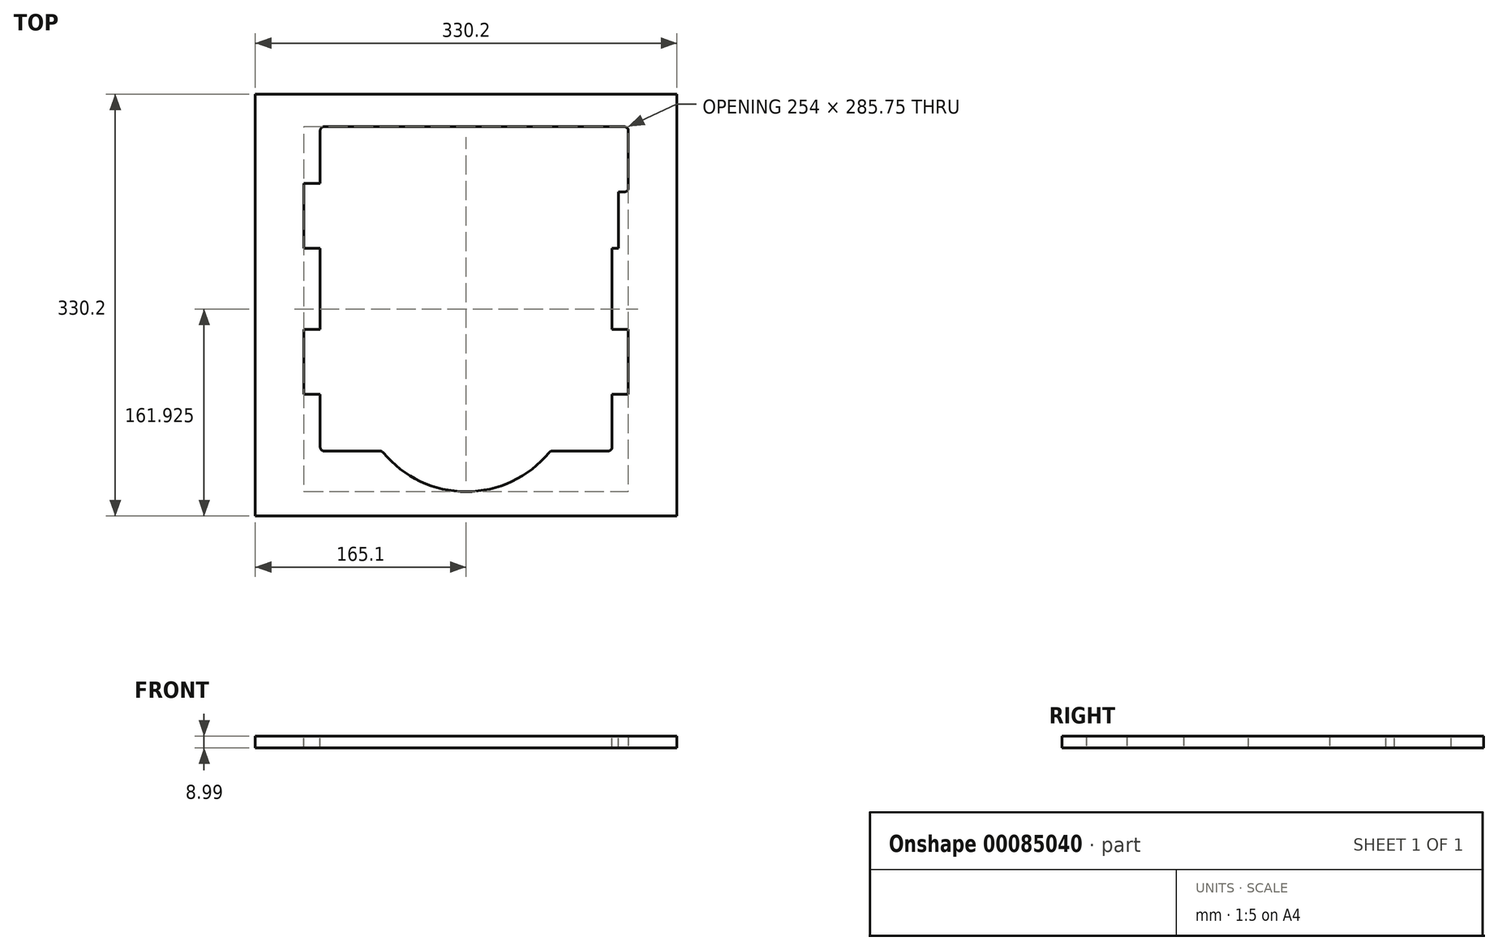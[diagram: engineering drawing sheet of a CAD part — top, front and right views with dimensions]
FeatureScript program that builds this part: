
annotation { "Feature Type Name" : "Feature", "Feature Type Description" : "" }
export const myFeature = defineFeature(function(context is Context, id is Id, definition is map)
    precondition{}
    {
        {
            var Q0;
            Q0=qCreatedBy(makeId("Top.planeOp"),FACE);
            var sketch = newSketch(context, id + "F0", { "sketchPlane" : qUnion([Q0])});
            skLineSegment(sketch, "E0.bottom", {"start": v(111.13, -114.3) * mm, "end": v(67.4, -114.3) * mm});
            skLineSegment(sketch, "E0.top", {"start": v(114.3, 114.3) * mm, "end": v(-111.13, 114.3) * mm});
            skLineSegment(sketch, "E0.left", {"start": v(114.3, -111.13) * mm, "end": v(114.3, 85.34) * mm});
            skLineSegment(sketch, "E0.right", {"start": v(-114.3, -111.13) * mm, "end": v(-114.3, 111.13) * mm});
            skPoint(sketch, "E0.middle", {"position": v(0, 0) * mm});
            skLineSegment(sketch, "E1.bottom", {"start": v(114.3, 114.3) * mm, "end": v(123.83, 114.3) * mm});
            skLineSegment(sketch, "E1.top", {"start": v(117.47, 88.52) * mm, "end": v(123.83, 88.52) * mm});
            skLineSegment(sketch, "E1.right", {"start": v(127, 111.13) * mm, "end": v(127, 91.7) * mm});
            skArc(sketch, "E2", {"start": v(-64.95, -115.45) * mm, "mid": v(0, -146.05) * mm, "end": v(64.95, -115.45) * mm});
            skLineSegment(sketch, "E3.trimOffspring", {"start": v(-67.4, -114.3) * mm, "end": v(-111.13, -114.3) * mm});
            skPoint(sketch, "E4.visualSharp", {"position": v(127, 114.3) * mm});
            skArc(sketch, "E4.filletArc", {"start": v(127, 111.13) * mm, "mid": v(126.07, 113.37) * mm, "end": v(123.83, 114.3) * mm});
            skPoint(sketch, "E5.visualSharp", {"position": v(127, 88.52) * mm});
            skArc(sketch, "E5.filletArc", {"start": v(123.83, 88.52) * mm, "mid": v(126.07, 89.45) * mm, "end": v(127, 91.7) * mm});
            skPoint(sketch, "E6.visualSharp", {"position": v(-114.3, 114.3) * mm});
            skArc(sketch, "E6.filletArc", {"start": v(-111.13, 114.3) * mm, "mid": v(-113.37, 113.37) * mm, "end": v(-114.3, 111.13) * mm});
            skPoint(sketch, "E7.visualSharp", {"position": v(-114.3, -114.3) * mm});
            skArc(sketch, "E7.filletArc", {"start": v(-114.3, -111.13) * mm, "mid": v(-113.37, -113.37) * mm, "end": v(-111.13, -114.3) * mm});
            skPoint(sketch, "E8.visualSharp", {"position": v(-65.88, -114.3) * mm});
            skArc(sketch, "E8.filletArc", {"start": v(-64.95, -115.45) * mm, "mid": v(-66.04, -114.6) * mm, "end": v(-67.4, -114.3) * mm});
            skPoint(sketch, "E9.visualSharp", {"position": v(65.88, -114.3) * mm});
            skArc(sketch, "E9.filletArc", {"start": v(67.4, -114.3) * mm, "mid": v(66.04, -114.6) * mm, "end": v(64.95, -115.45) * mm});
            skPoint(sketch, "E10.visualSharp", {"position": v(114.3, -114.3) * mm});
            skArc(sketch, "E10.filletArc", {"start": v(111.13, -114.3) * mm, "mid": v(113.37, -113.37) * mm, "end": v(114.3, -111.13) * mm});
            skPoint(sketch, "E11.visualSharp", {"position": v(114.3, 88.52) * mm});
            skArc(sketch, "E11.filletArc", {"start": v(117.47, 88.52) * mm, "mid": v(115.23, 87.59) * mm, "end": v(114.3, 85.34) * mm});
            skSolve(sketch);
        }
        {
            var Q0;
            Q0=makeQuery(id+"F0.imprint","IMPRINT",FACE,{"disambiguationData":[TD([[makeQuery(id+"F0.imprint","IMPRINT",EDGE,{"derivedFrom":sQuery(id+"F0.wireOp",EDGE,"E0.bottom")}),-1.0]])]});
            extrude(context, id + "F1", {"entities" : qUnion([Q0]), "depth" : 8.9 * mm});
        }
        {
            var Q0;
            Q0=makeQuery(id+"F1.opExtrude","SWEPT_FACE",FACE,{"disambiguationData":[OSD([sQuery(id+"F0.wireOp",EDGE,"E0.left")])]});
            var sketch = newSketch(context, id + "F2", { "sketchPlane" : qUnion([Q0])});
            skPoint(sketch, "E12.0", {"position": v(114.3, 0) * mm});
            skLineSegment(sketch, "E13", {"start": v(114.3, 0) * mm, "end": v(111.12, 0) * mm, "construction": true});
            skLineSegment(sketch, "E14", {"start": v(66.68, -3.18) * mm, "end": v(50.8, -3.18) * mm});
            skLineSegment(sketch, "E15", {"start": v(50.8, -3.17) * mm, "end": v(44.45, 0) * mm});
            skLineSegment(sketch, "E16", {"start": v(66.68, -3.17) * mm, "end": v(69.85, -4.76) * mm});
            skLineSegment(sketch, "E17.0", {"start": v(-111.13, 0) * mm, "end": v(44.45, 0) * mm});
            skPoint(sketch, "E18.orphan", {"position": v(111.12, 0) * mm});
            skLineSegment(sketch, "E19.0", {"start": v(51.4, -0.64) * mm, "end": v(44.45, 2.84) * mm});
            skLineSegment(sketch, "E19.1", {"start": v(67.27, -0.63) * mm, "end": v(51.4, -0.64) * mm});
            skLineSegment(sketch, "E19.2", {"start": v(67.27, -0.63) * mm, "end": v(69.85, -1.92) * mm});
            skLineSegment(sketch, "E20", {"start": v(44.45, 0) * mm, "end": v(44.45, 2.84) * mm});
            skLineSegment(sketch, "E21", {"start": v(69.85, -4.76) * mm, "end": v(69.85, -1.92) * mm});
            skSolve(sketch);
        }
        {
            var Q0;
            Q0=makeQuery(id+"F2.imprint","IMPRINT",FACE,{"disambiguationData":[TD([[makeQuery(id+"F2.imprint","IMPRINT",EDGE,{"derivedFrom":sQuery(id+"F2.wireOp",EDGE,"E14")}),-1.0]])]});
            var Q1;
            {var subQ0=sQuery(id+"F2.wireOp",EDGE,"E20");Q1=makeQuery(id+"F2.imprint","IMPRINT",FACE,{"disambiguationData":[TD([[makeQuery(id+"F2.imprint","IMPRINT",EDGE,{"derivedFrom":subQ0}),-1.0]])]});}
            extrude(context, id + "F3", {"entities" : qUnion([Q0, Q1]), "depth" : 4.93 * mm, "hasSecondDirection" : true, "secondDirectionOppositeDirection" : true, "secondDirectionDepth" : 2.54 * mm});
        }
        {
            var Q0;
            Q0=makeQuery(id+"F3.opExtrude","SWEPT_BODY",BODY,{"disambiguationData":[OSD([sQuery(id+"F0.wireOp",EDGE,"E0.left"),sQuery(id+"F2.wireOp",EDGE,"E14"),sQuery(id+"F2.wireOp",EDGE,"E15"),sQuery(id+"F2.wireOp",EDGE,"E16"),sQuery(id+"F2.wireOp",EDGE,"E19.0"),sQuery(id+"F2.wireOp",EDGE,"E19.1"),sQuery(id+"F2.wireOp",EDGE,"E19.2"),sQuery(id+"F2.wireOp",EDGE,"E21")])]});
            transform(context, id + "F4", {"entities" : qUnion([Q0]), "transformType" : TransformType.TRANSLATION_3D, "dx" : 0 * mm, "dy" : -114.3 * mm, "dz" : 0 * mm, "makeCopy" : true});
        }
        {
            var Q0;
            Q0=makeQuery(id+"F3.opExtrude","SWEPT_BODY",BODY,{"disambiguationData":[OSD([sQuery(id+"F0.wireOp",EDGE,"E0.left"),sQuery(id+"F2.wireOp",EDGE,"E14"),sQuery(id+"F2.wireOp",EDGE,"E15"),sQuery(id+"F2.wireOp",EDGE,"E16"),sQuery(id+"F2.wireOp",EDGE,"E19.0"),sQuery(id+"F2.wireOp",EDGE,"E19.1"),sQuery(id+"F2.wireOp",EDGE,"E19.2"),sQuery(id+"F2.wireOp",EDGE,"E21")])]});
            var Q1;
            Q1=makeQuery(id+"F4.opPattern","COPY",BODY,{"derivedFrom":makeQuery(id+"F3.opExtrude","SWEPT_BODY",BODY,{"disambiguationData":[OSD([sQuery(id+"F0.wireOp",EDGE,"E0.left"),sQuery(id+"F2.wireOp",EDGE,"E14"),sQuery(id+"F2.wireOp",EDGE,"E15"),sQuery(id+"F2.wireOp",EDGE,"E16"),sQuery(id+"F2.wireOp",EDGE,"E19.0"),sQuery(id+"F2.wireOp",EDGE,"E19.1"),sQuery(id+"F2.wireOp",EDGE,"E19.2"),sQuery(id+"F2.wireOp",EDGE,"E21")])]}),"instanceName":"1"});
            var Q2;
            Q2=qCreatedBy(makeId("Right.planeOp"),FACE);
            mirror(context, id + "F5", {"operationType" : NewBodyOperationType.ADD, "entities" : qUnion([Q0, Q1]), "mirrorPlane" : qUnion([Q2])});
        }
        {
            var Q0;
            Q0=makeQuery(id+"F1.opExtrude","CAP_FACE",FACE,{"disambiguationData":[OSD([sQuery(id+"F0.wireOp",EDGE,"E0.bottom"),sQuery(id+"F0.wireOp",EDGE,"E0.top"),sQuery(id+"F0.wireOp",EDGE,"E0.left"),sQuery(id+"F0.wireOp",EDGE,"E0.right"),sQuery(id+"F0.wireOp",EDGE,"E1.bottom"),sQuery(id+"F0.wireOp",EDGE,"E1.top"),sQuery(id+"F0.wireOp",EDGE,"E1.right"),sQuery(id+"F0.wireOp",EDGE,"E2"),sQuery(id+"F0.wireOp",EDGE,"E3.trimOffspring"),sQuery(id+"F0.wireOp",EDGE,"E4.filletArc"),sQuery(id+"F0.wireOp",EDGE,"E5.filletArc"),sQuery(id+"F0.wireOp",EDGE,"E6.filletArc"),sQuery(id+"F0.wireOp",EDGE,"E7.filletArc"),sQuery(id+"F0.wireOp",EDGE,"E8.filletArc"),sQuery(id+"F0.wireOp",EDGE,"E9.filletArc"),sQuery(id+"F0.wireOp",EDGE,"E10.filletArc"),sQuery(id+"F0.wireOp",EDGE,"E11.filletArc")])],"isStart":false});
            var sketch = newSketch(context, id + "F6", { "sketchPlane" : qUnion([Q0])});
            skLineSegment(sketch, "E22", {"start": v(-33.2, -114.3) * mm, "end": v(33.2, -114.3) * mm});
            skLineSegment(sketch, "E23", {"start": v(0, -114.3) * mm, "end": v(0, -138.11) * mm, "construction": true});
            skPoint(sketch, "E23.endSnap0", {"position": v(0, -114.3) * mm});
            skArc(sketch, "E24", {"start": v(-36.66, -122.34) * mm, "mid": v(0, -138.11) * mm, "end": v(36.66, -122.34) * mm});
            skPoint(sketch, "E25.visualSharp", {"position": v(-42.86, -114.3) * mm});
            skArc(sketch, "E25.filletArc", {"start": v(-33.2, -114.3) * mm, "mid": v(-37.58, -117.18) * mm, "end": v(-36.66, -122.34) * mm});
            skPoint(sketch, "E26.visualSharp", {"position": v(42.86, -114.3) * mm});
            skArc(sketch, "E26.filletArc", {"start": v(36.66, -122.34) * mm, "mid": v(37.58, -117.18) * mm, "end": v(33.2, -114.3) * mm});
            skSolve(sketch);
        }
        {
            var Q0;
            Q0=makeQuery(id+"F6.imprint","IMPRINT",FACE,{"disambiguationData":[TD([[makeQuery(id+"F6.imprint","IMPRINT",EDGE,{"derivedFrom":sQuery(id+"F6.wireOp",EDGE,"E22")}),-1.0]])]});
            extrude(context, id + "F7", {"entities" : qUnion([Q0]), "operationType" : NewBodyOperationType.REMOVE, "endBound" : BoundingType.THROUGH_ALL, "oppositeDirection" : true, "depth" : 25.4 * mm});
        }
        {
            var Q0;
            Q0=qCreatedBy(makeId("Top.planeOp"),FACE);
            var sketch = newSketch(context, id + "F8", { "sketchPlane" : qUnion([Q0])});
            skLineSegment(sketch, "E27.bottom", {"start": v(165.1, -165.1) * mm, "end": v(-165.1, -165.1) * mm});
            skLineSegment(sketch, "E27.top", {"start": v(165.1, 165.1) * mm, "end": v(-165.1, 165.1) * mm});
            skLineSegment(sketch, "E27.left", {"start": v(165.1, -165.1) * mm, "end": v(165.1, 165.1) * mm});
            skLineSegment(sketch, "E27.right", {"start": v(-165.1, -165.1) * mm, "end": v(-165.1, 165.1) * mm});
            skPoint(sketch, "E27.middle", {"position": v(0, 0) * mm});
            skLineSegment(sketch, "E28.0", {"start": v(-111.13, 114.3) * mm, "end": v(123.83, 114.3) * mm});
            skArc(sketch, "E29.0", {"start": v(-111.13, 114.3) * mm, "mid": v(-113.37, 113.37) * mm, "end": v(-114.3, 111.13) * mm});
            skLineSegment(sketch, "E30.0", {"start": v(-114.3, -111.13) * mm, "end": v(-114.3, 111.13) * mm});
            skLineSegment(sketch, "E31.0", {"start": v(-119.23, 69.85) * mm, "end": v(-114.3, 69.85) * mm});
            skLineSegment(sketch, "E32.0", {"start": v(-119.23, 67.27) * mm, "end": v(-119.23, 69.85) * mm});
            skLineSegment(sketch, "E33.0", {"start": v(-119.23, 67.27) * mm, "end": v(-119.23, 51.4) * mm});
            skLineSegment(sketch, "E34.0", {"start": v(-119.23, 51.4) * mm, "end": v(-119.23, 44.45) * mm});
            skLineSegment(sketch, "E35.0", {"start": v(-119.23, 44.45) * mm, "end": v(-114.3, 44.45) * mm});
            skLineSegment(sketch, "E36.0", {"start": v(-119.23, -44.45) * mm, "end": v(-114.3, -44.45) * mm});
            skLineSegment(sketch, "E37.0", {"start": v(-119.23, -47.03) * mm, "end": v(-119.23, -44.45) * mm});
            skLineSegment(sketch, "E38.0", {"start": v(-119.23, -47.03) * mm, "end": v(-119.23, -62.9) * mm});
            skLineSegment(sketch, "E39.0", {"start": v(-119.23, -62.9) * mm, "end": v(-119.23, -69.85) * mm});
            skLineSegment(sketch, "E40.0", {"start": v(-119.23, -69.85) * mm, "end": v(-114.3, -69.85) * mm});
            skArc(sketch, "E41.0", {"start": v(-114.3, -111.13) * mm, "mid": v(-113.37, -113.37) * mm, "end": v(-111.13, -114.3) * mm});
            skLineSegment(sketch, "E42.0", {"start": v(-67.4, -114.3) * mm, "end": v(-111.13, -114.3) * mm});
            skArc(sketch, "E43.0", {"start": v(-64.95, -115.45) * mm, "mid": v(0, -146.05) * mm, "end": v(64.95, -115.45) * mm});
            skArc(sketch, "E44.0", {"start": v(67.4, -114.3) * mm, "mid": v(66.04, -114.6) * mm, "end": v(64.95, -115.45) * mm});
            skLineSegment(sketch, "E45.0", {"start": v(111.13, -114.3) * mm, "end": v(67.4, -114.3) * mm});
            skArc(sketch, "E46.0", {"start": v(111.13, -114.3) * mm, "mid": v(113.37, -113.37) * mm, "end": v(114.3, -111.13) * mm});
            skLineSegment(sketch, "E47.0", {"start": v(114.3, -111.13) * mm, "end": v(114.3, 85.34) * mm});
            skLineSegment(sketch, "E48.0", {"start": v(119.23, -69.85) * mm, "end": v(114.3, -69.85) * mm});
            skLineSegment(sketch, "E49.0", {"start": v(119.23, -62.9) * mm, "end": v(119.23, -69.85) * mm});
            skLineSegment(sketch, "E50.0", {"start": v(119.23, -47.03) * mm, "end": v(119.23, -62.9) * mm});
            skLineSegment(sketch, "E51.0", {"start": v(119.23, -47.03) * mm, "end": v(119.23, -44.45) * mm});
            skLineSegment(sketch, "E52.0", {"start": v(119.23, -44.45) * mm, "end": v(114.3, -44.45) * mm});
            skLineSegment(sketch, "E53.0", {"start": v(119.23, 44.45) * mm, "end": v(114.3, 44.45) * mm});
            skLineSegment(sketch, "E54.0", {"start": v(119.23, 51.4) * mm, "end": v(119.23, 44.45) * mm});
            skLineSegment(sketch, "E55.0", {"start": v(119.23, 67.27) * mm, "end": v(119.23, 51.4) * mm});
            skLineSegment(sketch, "E56.0", {"start": v(119.23, 67.27) * mm, "end": v(119.23, 69.85) * mm});
            skLineSegment(sketch, "E57.0", {"start": v(119.23, 69.85) * mm, "end": v(114.3, 69.85) * mm});
            skArc(sketch, "E58.0", {"start": v(117.47, 88.52) * mm, "mid": v(115.23, 87.59) * mm, "end": v(114.3, 85.34) * mm});
            skLineSegment(sketch, "E59.0", {"start": v(117.47, 88.52) * mm, "end": v(123.83, 88.52) * mm});
            skArc(sketch, "E60.0", {"start": v(123.83, 88.52) * mm, "mid": v(126.07, 89.45) * mm, "end": v(127, 91.7) * mm});
            skLineSegment(sketch, "E61.0", {"start": v(127, 111.13) * mm, "end": v(127, 91.7) * mm});
            skArc(sketch, "E62.0", {"start": v(127, 111.13) * mm, "mid": v(126.07, 113.37) * mm, "end": v(123.83, 114.3) * mm});
            skPoint(sketch, "E63.orphan", {"position": v(-111.76, 69.85) * mm});
            skPoint(sketch, "E64.orphan", {"position": v(111.76, 69.85) * mm});
            skPoint(sketch, "E65.orphan", {"position": v(111.76, -44.45) * mm});
            skPoint(sketch, "E66.orphan", {"position": v(-111.76, -44.45) * mm});
            skPoint(sketch, "E67.orphan", {"position": v(-111.76, -62.9) * mm});
            skArc(sketch, "E68.0", {"start": v(-64.95, -115.45) * mm, "mid": v(-66.04, -114.6) * mm, "end": v(-67.4, -114.3) * mm});
            skSolve(sketch);
        }
        {
            var Q0;
            Q0=makeQuery(id+"F8.imprint","IMPRINT",FACE,{"disambiguationData":[TD([[makeQuery(id+"F8.imprint","IMPRINT",EDGE,{"derivedFrom":sQuery(id+"F8.wireOp",EDGE,"E27.bottom")}),-1.0]])]});
            extrude(context, id + "F9", {"entities" : qUnion([Q0]), "depth" : 9 * mm});
        }
        {
            var Q0;
            Q0=makeQuery(id+"F1.opExtrude","SWEPT_BODY",BODY,{"disambiguationData":[OSD([sQuery(id+"F0.wireOp",EDGE,"E0.bottom"),sQuery(id+"F0.wireOp",EDGE,"E0.top"),sQuery(id+"F0.wireOp",EDGE,"E0.left"),sQuery(id+"F0.wireOp",EDGE,"E0.right"),sQuery(id+"F0.wireOp",EDGE,"E1.bottom"),sQuery(id+"F0.wireOp",EDGE,"E1.top"),sQuery(id+"F0.wireOp",EDGE,"E1.right"),sQuery(id+"F0.wireOp",EDGE,"E2"),sQuery(id+"F0.wireOp",EDGE,"E3.trimOffspring"),sQuery(id+"F0.wireOp",EDGE,"E4.filletArc"),sQuery(id+"F0.wireOp",EDGE,"E5.filletArc"),sQuery(id+"F0.wireOp",EDGE,"E6.filletArc"),sQuery(id+"F0.wireOp",EDGE,"E7.filletArc"),sQuery(id+"F0.wireOp",EDGE,"E8.filletArc"),sQuery(id+"F0.wireOp",EDGE,"E9.filletArc"),sQuery(id+"F0.wireOp",EDGE,"E10.filletArc"),sQuery(id+"F0.wireOp",EDGE,"E11.filletArc")])]});
            transform(context, id + "F10", {"entities" : qUnion([Q0]), "transformType" : TransformType.TRANSLATION_3D, "dx" : 0 * mm, "dy" : 25.4 * mm, "dz" : 0 * mm, "makeCopy" : false});
        }
        {
            var Q0;
            Q0=makeQuery(id+"F9.opExtrude","CAP_FACE",FACE,{"disambiguationData":[OSD([sQuery(id+"F8.wireOp",EDGE,"E27.bottom"),sQuery(id+"F8.wireOp",EDGE,"E27.top"),sQuery(id+"F8.wireOp",EDGE,"E27.left"),sQuery(id+"F8.wireOp",EDGE,"E27.right"),sQuery(id+"F8.wireOp",EDGE,"E28.0"),sQuery(id+"F8.wireOp",EDGE,"E29.0"),sQuery(id+"F8.wireOp",EDGE,"E30.0"),sQuery(id+"F8.wireOp",EDGE,"E31.0"),sQuery(id+"F8.wireOp",EDGE,"E32.0"),sQuery(id+"F8.wireOp",EDGE,"E33.0"),sQuery(id+"F8.wireOp",EDGE,"E34.0"),sQuery(id+"F8.wireOp",EDGE,"E35.0"),sQuery(id+"F8.wireOp",EDGE,"E36.0"),sQuery(id+"F8.wireOp",EDGE,"E37.0"),sQuery(id+"F8.wireOp",EDGE,"E38.0"),sQuery(id+"F8.wireOp",EDGE,"E39.0"),sQuery(id+"F8.wireOp",EDGE,"E40.0"),sQuery(id+"F8.wireOp",EDGE,"E41.0"),sQuery(id+"F8.wireOp",EDGE,"E42.0"),sQuery(id+"F8.wireOp",EDGE,"E43.0"),sQuery(id+"F8.wireOp",EDGE,"E44.0"),sQuery(id+"F8.wireOp",EDGE,"E45.0"),sQuery(id+"F8.wireOp",EDGE,"E46.0"),sQuery(id+"F8.wireOp",EDGE,"E47.0"),sQuery(id+"F8.wireOp",EDGE,"E48.0"),sQuery(id+"F8.wireOp",EDGE,"E49.0"),sQuery(id+"F8.wireOp",EDGE,"E50.0"),sQuery(id+"F8.wireOp",EDGE,"E51.0"),sQuery(id+"F8.wireOp",EDGE,"E52.0"),sQuery(id+"F8.wireOp",EDGE,"E53.0"),sQuery(id+"F8.wireOp",EDGE,"E54.0"),sQuery(id+"F8.wireOp",EDGE,"E55.0"),sQuery(id+"F8.wireOp",EDGE,"E56.0"),sQuery(id+"F8.wireOp",EDGE,"E57.0"),sQuery(id+"F8.wireOp",EDGE,"E58.0"),sQuery(id+"F8.wireOp",EDGE,"E59.0"),sQuery(id+"F8.wireOp",EDGE,"E60.0"),sQuery(id+"F8.wireOp",EDGE,"E61.0"),sQuery(id+"F8.wireOp",EDGE,"E62.0"),sQuery(id+"F8.wireOp",EDGE,"E68.0")])],"isStart":false});
            var sketch = newSketch(context, id + "F11", { "sketchPlane" : qUnion([Q0])});
            skLineSegment(sketch, "E69.0", {"start": v(117.47, 113.92) * mm, "end": v(123.83, 113.92) * mm});
            skArc(sketch, "E70.0", {"start": v(123.83, 113.92) * mm, "mid": v(126.07, 114.85) * mm, "end": v(127, 117.1) * mm});
            skLineSegment(sketch, "E71.0", {"start": v(127, 136.53) * mm, "end": v(127, 117.1) * mm});
            skArc(sketch, "E72.0", {"start": v(127, 136.53) * mm, "mid": v(126.07, 138.77) * mm, "end": v(123.83, 139.7) * mm});
            skLineSegment(sketch, "E73.0", {"start": v(-111.13, 139.7) * mm, "end": v(123.83, 139.7) * mm});
            skArc(sketch, "E74.0", {"start": v(-111.13, 139.7) * mm, "mid": v(-113.37, 138.77) * mm, "end": v(-114.3, 136.53) * mm});
            skLineSegment(sketch, "E75.0", {"start": v(-114.3, -85.73) * mm, "end": v(-114.3, 136.53) * mm});
            skLineSegment(sketch, "E76.0", {"start": v(-119.23, 95.25) * mm, "end": v(-111.76, 95.25) * mm});
            skLineSegment(sketch, "E77.0", {"start": v(-119.23, 92.67) * mm, "end": v(-119.23, 95.25) * mm});
            skLineSegment(sketch, "E78.0", {"start": v(-119.23, 92.67) * mm, "end": v(-119.23, 76.8) * mm});
            skLineSegment(sketch, "E79.0", {"start": v(-119.23, 76.8) * mm, "end": v(-119.23, 69.85) * mm});
            skLineSegment(sketch, "E80.0", {"start": v(-119.23, 69.85) * mm, "end": v(-114.3, 69.85) * mm});
            skLineSegment(sketch, "E81.0", {"start": v(-119.23, -19.05) * mm, "end": v(-111.76, -19.05) * mm});
            skLineSegment(sketch, "E82.0", {"start": v(-119.23, -21.63) * mm, "end": v(-119.23, -19.05) * mm});
            skLineSegment(sketch, "E83.0", {"start": v(-119.23, -21.63) * mm, "end": v(-119.23, -37.5) * mm});
            skLineSegment(sketch, "E84.0", {"start": v(-119.23, -37.5) * mm, "end": v(-119.23, -44.45) * mm});
            skLineSegment(sketch, "E85.0", {"start": v(-119.23, -44.45) * mm, "end": v(-114.3, -44.45) * mm});
            skLineSegment(sketch, "E86.0", {"start": v(119.23, -44.45) * mm, "end": v(114.3, -44.45) * mm});
            skLineSegment(sketch, "E87.0", {"start": v(119.23, -37.5) * mm, "end": v(119.23, -44.45) * mm});
            skLineSegment(sketch, "E88.0", {"start": v(119.23, -21.63) * mm, "end": v(119.23, -37.5) * mm});
            skLineSegment(sketch, "E89.0", {"start": v(119.23, -21.63) * mm, "end": v(119.23, -19.05) * mm});
            skLineSegment(sketch, "E90.0", {"start": v(119.23, -19.05) * mm, "end": v(111.76, -19.05) * mm});
            skLineSegment(sketch, "E91.0", {"start": v(114.3, -85.73) * mm, "end": v(114.3, 110.74) * mm});
            skLineSegment(sketch, "E92.0", {"start": v(119.23, 69.85) * mm, "end": v(114.3, 69.85) * mm});
            skLineSegment(sketch, "E93.0", {"start": v(119.23, 76.8) * mm, "end": v(119.23, 69.85) * mm});
            skLineSegment(sketch, "E94.0", {"start": v(119.23, 92.67) * mm, "end": v(119.23, 76.8) * mm});
            skLineSegment(sketch, "E95.0", {"start": v(119.23, 92.67) * mm, "end": v(119.23, 95.25) * mm});
            skLineSegment(sketch, "E96.0", {"start": v(119.23, 95.25) * mm, "end": v(111.76, 95.25) * mm});
            skArc(sketch, "E97.0", {"start": v(117.47, 113.92) * mm, "mid": v(115.23, 112.99) * mm, "end": v(114.3, 110.74) * mm});
            skLineSegment(sketch, "E98.0", {"start": v(-67.4, -88.9) * mm, "end": v(-111.13, -88.9) * mm});
            skArc(sketch, "E99.0", {"start": v(-114.3, -85.73) * mm, "mid": v(-113.37, -87.97) * mm, "end": v(-111.13, -88.9) * mm});
            skArc(sketch, "E100.0", {"start": v(-64.95, -90.05) * mm, "mid": v(-66.04, -89.2) * mm, "end": v(-67.4, -88.9) * mm});
            skArc(sketch, "E101.0", {"start": v(-64.95, -90.05) * mm, "mid": v(0, -120.65) * mm, "end": v(64.95, -90.05) * mm});
            skArc(sketch, "E102.0", {"start": v(111.13, -88.9) * mm, "mid": v(113.37, -87.97) * mm, "end": v(114.3, -85.73) * mm});
            skLineSegment(sketch, "E103.0", {"start": v(111.13, -88.9) * mm, "end": v(67.4, -88.9) * mm});
            skArc(sketch, "E104.0", {"start": v(67.4, -88.9) * mm, "mid": v(66.04, -89.2) * mm, "end": v(64.95, -90.05) * mm});
            skSolve(sketch);
        }
        {
            var Q0;
            Q0=makeQuery(id+"F1.opExtrude","SWEPT_BODY",BODY,{"disambiguationData":[OSD([sQuery(id+"F0.wireOp",EDGE,"E0.bottom"),sQuery(id+"F0.wireOp",EDGE,"E0.top"),sQuery(id+"F0.wireOp",EDGE,"E0.left"),sQuery(id+"F0.wireOp",EDGE,"E0.right"),sQuery(id+"F0.wireOp",EDGE,"E1.bottom"),sQuery(id+"F0.wireOp",EDGE,"E1.top"),sQuery(id+"F0.wireOp",EDGE,"E1.right"),sQuery(id+"F0.wireOp",EDGE,"E2"),sQuery(id+"F0.wireOp",EDGE,"E3.trimOffspring"),sQuery(id+"F0.wireOp",EDGE,"E4.filletArc"),sQuery(id+"F0.wireOp",EDGE,"E5.filletArc"),sQuery(id+"F0.wireOp",EDGE,"E6.filletArc"),sQuery(id+"F0.wireOp",EDGE,"E7.filletArc"),sQuery(id+"F0.wireOp",EDGE,"E8.filletArc"),sQuery(id+"F0.wireOp",EDGE,"E9.filletArc"),sQuery(id+"F0.wireOp",EDGE,"E10.filletArc"),sQuery(id+"F0.wireOp",EDGE,"E11.filletArc")])]});
            deleteBodies(context, id + "F12", {"entities" : qUnion([Q0])});
        }
        {
            var Q0;
            {var subQ1=sQuery(id+"F11.wireOp",EDGE,"E71.0");Q0=makeQuery(id+"F11.imprint","IMPRINT",FACE,{"disambiguationData":[TD([[makeQuery(id+"F11.imprint","IMPRINT",EDGE,{"derivedFrom":subQ1}),-1.0]])]});}
            var Q1;
            {var subQ0=sQuery(id+"F11.wireOp",EDGE,"E77.0");Q1=makeQuery(id+"F11.imprint","IMPRINT",FACE,{"disambiguationData":[TD([[makeQuery(id+"F11.imprint","IMPRINT",EDGE,{"derivedFrom":subQ0}),-1.0]])]});}
            var Q2;
            {var subQ0=sQuery(id+"F11.wireOp",EDGE,"E82.0");Q2=makeQuery(id+"F11.imprint","IMPRINT",FACE,{"disambiguationData":[TD([[makeQuery(id+"F11.imprint","IMPRINT",EDGE,{"derivedFrom":subQ0}),-1.0]])]});}
            var Q3;
            {var subQ2=sQuery(id+"F11.wireOp",EDGE,"E86.0");Q3=makeQuery(id+"F11.imprint","IMPRINT",FACE,{"disambiguationData":[TD([[makeQuery(id+"F11.imprint","IMPRINT",EDGE,{"derivedFrom":subQ2}),-1.0]])]});}
            var Q4;
            {var subQ1=sQuery(id+"F11.wireOp",EDGE,"E92.0");Q4=makeQuery(id+"F11.imprint","IMPRINT",FACE,{"disambiguationData":[TD([[makeQuery(id+"F11.imprint","IMPRINT",EDGE,{"derivedFrom":subQ1}),-1.0]])]});}
            extrude(context, id + "F13", {"entities" : qUnion([Q0, Q1, Q2, Q3, Q4]), "operationType" : NewBodyOperationType.REMOVE, "oppositeDirection" : true, "depth" : 25.4 * mm});
        }
        {
            var Q0;
            Q0=makeQuery(id+"F9.opExtrude","CAP_FACE",FACE,{"disambiguationData":[OSD([sQuery(id+"F8.wireOp",EDGE,"E27.bottom"),sQuery(id+"F8.wireOp",EDGE,"E27.top"),sQuery(id+"F8.wireOp",EDGE,"E27.left"),sQuery(id+"F8.wireOp",EDGE,"E27.right"),sQuery(id+"F8.wireOp",EDGE,"E28.0"),sQuery(id+"F8.wireOp",EDGE,"E29.0"),sQuery(id+"F8.wireOp",EDGE,"E30.0"),sQuery(id+"F8.wireOp",EDGE,"E31.0"),sQuery(id+"F8.wireOp",EDGE,"E32.0"),sQuery(id+"F8.wireOp",EDGE,"E33.0"),sQuery(id+"F8.wireOp",EDGE,"E34.0"),sQuery(id+"F8.wireOp",EDGE,"E35.0"),sQuery(id+"F8.wireOp",EDGE,"E36.0"),sQuery(id+"F8.wireOp",EDGE,"E37.0"),sQuery(id+"F8.wireOp",EDGE,"E38.0"),sQuery(id+"F8.wireOp",EDGE,"E39.0"),sQuery(id+"F8.wireOp",EDGE,"E40.0"),sQuery(id+"F8.wireOp",EDGE,"E41.0"),sQuery(id+"F8.wireOp",EDGE,"E42.0"),sQuery(id+"F8.wireOp",EDGE,"E43.0"),sQuery(id+"F8.wireOp",EDGE,"E44.0"),sQuery(id+"F8.wireOp",EDGE,"E45.0"),sQuery(id+"F8.wireOp",EDGE,"E46.0"),sQuery(id+"F8.wireOp",EDGE,"E47.0"),sQuery(id+"F8.wireOp",EDGE,"E48.0"),sQuery(id+"F8.wireOp",EDGE,"E49.0"),sQuery(id+"F8.wireOp",EDGE,"E50.0"),sQuery(id+"F8.wireOp",EDGE,"E51.0"),sQuery(id+"F8.wireOp",EDGE,"E52.0"),sQuery(id+"F8.wireOp",EDGE,"E53.0"),sQuery(id+"F8.wireOp",EDGE,"E54.0"),sQuery(id+"F8.wireOp",EDGE,"E55.0"),sQuery(id+"F8.wireOp",EDGE,"E56.0"),sQuery(id+"F8.wireOp",EDGE,"E57.0"),sQuery(id+"F8.wireOp",EDGE,"E58.0"),sQuery(id+"F8.wireOp",EDGE,"E59.0"),sQuery(id+"F8.wireOp",EDGE,"E60.0"),sQuery(id+"F8.wireOp",EDGE,"E61.0"),sQuery(id+"F8.wireOp",EDGE,"E62.0"),sQuery(id+"F8.wireOp",EDGE,"E68.0")])],"isStart":false});
            var sketch = newSketch(context, id + "F14", { "sketchPlane" : qUnion([Q0])});
            skLineSegment(sketch, "E105", {"start": v(127, 117.1) * mm, "end": v(127, 111.13) * mm});
            skLineSegment(sketch, "E106", {"start": v(127, 111.13) * mm, "end": v(124.9, 111.13) * mm});
            skLineSegment(sketch, "E107", {"start": v(124.9, 111.13) * mm, "end": v(124.9, 117.1) * mm});
            skLineSegment(sketch, "E108", {"start": v(124.9, 117.1) * mm, "end": v(127, 117.1) * mm});
            skSolve(sketch);
        }
        {
            var Q0;
            Q0=makeQuery(id+"F14.imprint","IMPRINT",FACE,{"disambiguationData":[TD([[makeQuery(id+"F14.imprint","IMPRINT",EDGE,{"derivedFrom":sQuery(id+"F14.wireOp",EDGE,"E105")}),-1.0]])]});
            extrude(context, id + "F15", {"entities" : qUnion([Q0]), "operationType" : NewBodyOperationType.REMOVE, "endBound" : BoundingType.THROUGH_ALL, "oppositeDirection" : true, "depth" : 25.4 * mm});
        }
        {
            var Q0;
            Q0=makeQuery(id+"F9.opExtrude","CAP_FACE",FACE,{"disambiguationData":[OSD([sQuery(id+"F8.wireOp",EDGE,"E27.bottom"),sQuery(id+"F8.wireOp",EDGE,"E27.top"),sQuery(id+"F8.wireOp",EDGE,"E27.left"),sQuery(id+"F8.wireOp",EDGE,"E27.right"),sQuery(id+"F8.wireOp",EDGE,"E28.0"),sQuery(id+"F8.wireOp",EDGE,"E29.0"),sQuery(id+"F8.wireOp",EDGE,"E30.0"),sQuery(id+"F8.wireOp",EDGE,"E31.0"),sQuery(id+"F8.wireOp",EDGE,"E32.0"),sQuery(id+"F8.wireOp",EDGE,"E33.0"),sQuery(id+"F8.wireOp",EDGE,"E34.0"),sQuery(id+"F8.wireOp",EDGE,"E35.0"),sQuery(id+"F8.wireOp",EDGE,"E36.0"),sQuery(id+"F8.wireOp",EDGE,"E37.0"),sQuery(id+"F8.wireOp",EDGE,"E38.0"),sQuery(id+"F8.wireOp",EDGE,"E39.0"),sQuery(id+"F8.wireOp",EDGE,"E40.0"),sQuery(id+"F8.wireOp",EDGE,"E41.0"),sQuery(id+"F8.wireOp",EDGE,"E42.0"),sQuery(id+"F8.wireOp",EDGE,"E43.0"),sQuery(id+"F8.wireOp",EDGE,"E44.0"),sQuery(id+"F8.wireOp",EDGE,"E45.0"),sQuery(id+"F8.wireOp",EDGE,"E46.0"),sQuery(id+"F8.wireOp",EDGE,"E47.0"),sQuery(id+"F8.wireOp",EDGE,"E48.0"),sQuery(id+"F8.wireOp",EDGE,"E49.0"),sQuery(id+"F8.wireOp",EDGE,"E50.0"),sQuery(id+"F8.wireOp",EDGE,"E51.0"),sQuery(id+"F8.wireOp",EDGE,"E52.0"),sQuery(id+"F8.wireOp",EDGE,"E53.0"),sQuery(id+"F8.wireOp",EDGE,"E54.0"),sQuery(id+"F8.wireOp",EDGE,"E55.0"),sQuery(id+"F8.wireOp",EDGE,"E56.0"),sQuery(id+"F8.wireOp",EDGE,"E57.0"),sQuery(id+"F8.wireOp",EDGE,"E58.0"),sQuery(id+"F8.wireOp",EDGE,"E59.0"),sQuery(id+"F8.wireOp",EDGE,"E60.0"),sQuery(id+"F8.wireOp",EDGE,"E61.0"),sQuery(id+"F8.wireOp",EDGE,"E62.0"),sQuery(id+"F8.wireOp",EDGE,"E68.0")])],"isStart":false});
            var sketch = newSketch(context, id + "F16", { "sketchPlane" : qUnion([Q0])});
            skLineSegment(sketch, "E109.bottom", {"start": v(119.23, 44.45) * mm, "end": v(127, 44.45) * mm});
            skLineSegment(sketch, "E109.top", {"start": v(119.23, 91.7) * mm, "end": v(127, 91.7) * mm});
            skLineSegment(sketch, "E109.left", {"start": v(119.23, 44.45) * mm, "end": v(119.23, 91.7) * mm});
            skLineSegment(sketch, "E109.right", {"start": v(127, 44.45) * mm, "end": v(127, 91.7) * mm});
            skLineSegment(sketch, "E110.bottom", {"start": v(127, 44.45) * mm, "end": v(114.3, 44.45) * mm, "construction": true});
            skLineSegment(sketch, "E110.top", {"start": v(127, -19.05) * mm, "end": v(114.3, -19.05) * mm, "construction": true});
            skLineSegment(sketch, "E110.left", {"start": v(127, 44.45) * mm, "end": v(127, -19.05) * mm, "construction": true});
            skLineSegment(sketch, "E110.right", {"start": v(114.3, 44.45) * mm, "end": v(114.3, -19.05) * mm, "construction": true});
            skLineSegment(sketch, "E111.bottom", {"start": v(127, -19.05) * mm, "end": v(114.3, -19.05) * mm});
            skLineSegment(sketch, "E111.top", {"start": v(127, -69.85) * mm, "end": v(114.3, -69.85) * mm});
            skLineSegment(sketch, "E111.left", {"start": v(127, -19.05) * mm, "end": v(127, -69.85) * mm});
            skLineSegment(sketch, "E111.right", {"start": v(114.3, -19.05) * mm, "end": v(114.3, -69.85) * mm});
            skLineSegment(sketch, "E112.bottom", {"start": v(-114.3, 95.25) * mm, "end": v(-127, 95.25) * mm});
            skLineSegment(sketch, "E112.top", {"start": v(-114.3, 44.45) * mm, "end": v(-127, 44.45) * mm});
            skLineSegment(sketch, "E112.left", {"start": v(-114.3, 95.25) * mm, "end": v(-114.3, 44.45) * mm});
            skLineSegment(sketch, "E112.right", {"start": v(-127, 95.25) * mm, "end": v(-127, 44.45) * mm});
            skLineSegment(sketch, "E113.bottom", {"start": v(-114.3, -19.05) * mm, "end": v(-127, -19.05) * mm});
            skLineSegment(sketch, "E113.top", {"start": v(-114.3, -69.85) * mm, "end": v(-127, -69.85) * mm});
            skLineSegment(sketch, "E113.left", {"start": v(-114.3, -19.05) * mm, "end": v(-114.3, -69.85) * mm});
            skLineSegment(sketch, "E113.right", {"start": v(-127, -19.05) * mm, "end": v(-127, -69.85) * mm});
            skLineSegment(sketch, "E114.bottom", {"start": v(119.23, 44.45) * mm, "end": v(120.65, 44.45) * mm});
            skLineSegment(sketch, "E114.top", {"start": v(119.23, 91.7) * mm, "end": v(120.65, 91.7) * mm});
            skLineSegment(sketch, "E114.right", {"start": v(120.65, 44.45) * mm, "end": v(120.65, 91.7) * mm});
            skSolve(sketch);
        }
        {
            var Q0;
            {var subQ2=sQuery(id+"F16.wireOp",EDGE,"E112.right");Q0=makeQuery(id+"F16.imprint","IMPRINT",FACE,{"disambiguationData":[TD([[makeQuery(id+"F16.imprint","IMPRINT",EDGE,{"derivedFrom":subQ2}),1.0]])]});}
            var Q1;
            {var subQ2=sQuery(id+"F16.wireOp",EDGE,"E113.right");Q1=makeQuery(id+"F16.imprint","IMPRINT",FACE,{"disambiguationData":[TD([[makeQuery(id+"F16.imprint","IMPRINT",EDGE,{"derivedFrom":subQ2}),1.0]])]});}
            var Q2;
            {var subQ2=sQuery(id+"F16.wireOp",EDGE,"E111.left");Q2=makeQuery(id+"F16.imprint","IMPRINT",FACE,{"disambiguationData":[TD([[makeQuery(id+"F16.imprint","IMPRINT",EDGE,{"derivedFrom":subQ2}),-1.0]])]});}
            var Q3;
            {var subQ0=sQuery(id+"F16.wireOp",EDGE,"E114.bottom");Q3=makeQuery(id+"F16.imprint","IMPRINT",FACE,{"disambiguationData":[TD([[makeQuery(id+"F16.imprint","IMPRINT",EDGE,{"derivedFrom":subQ0}),1.0]])]});}
            extrude(context, id + "F17", {"entities" : qUnion([Q0, Q1, Q2, Q3]), "operationType" : NewBodyOperationType.REMOVE, "endBound" : BoundingType.THROUGH_ALL, "oppositeDirection" : true, "depth" : 25.4 * mm});
        }
    });
